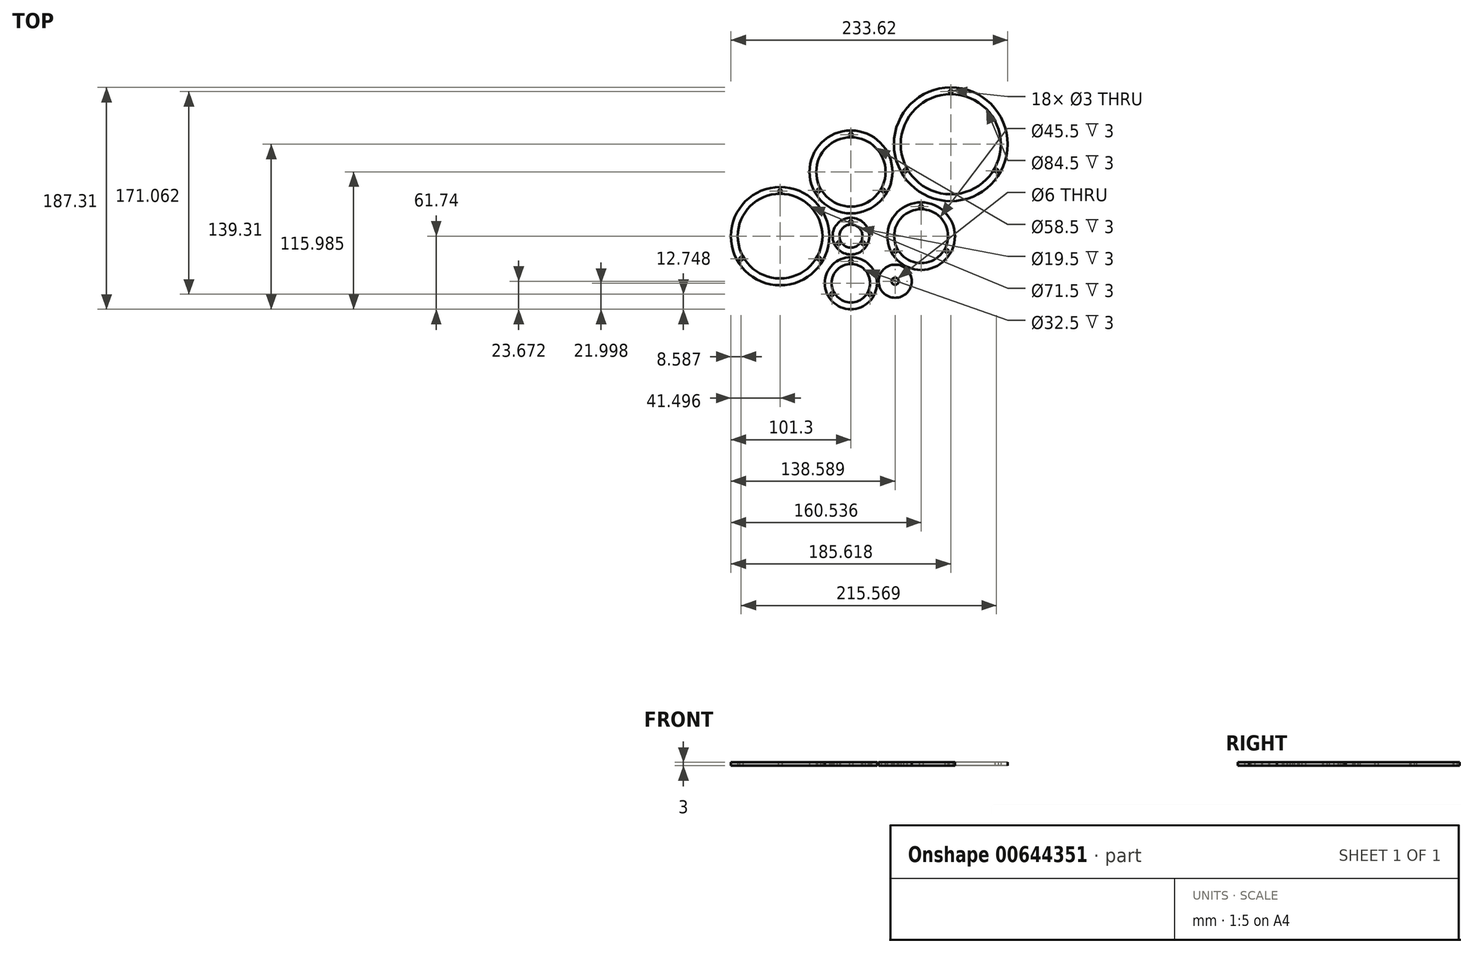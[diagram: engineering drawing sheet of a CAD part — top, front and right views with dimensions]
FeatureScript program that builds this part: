
annotation { "Feature Type Name" : "Feature", "Feature Type Description" : "" }
export const myFeature = defineFeature(function(context is Context, id is Id, definition is map)
    precondition{}
    {
        {
            var Q0;
            Q0=qCreatedBy(makeId("Top.planeOp"),FACE);
            var sketch = newSketch(context, id + "F0", { "sketchPlane" : qUnion([Q0])});
            skCircle(sketch, "E0", {"center": v(37.29, -38.07) * mm, "radius": 14 * mm});
            skCircle(sketch, "E1", {"center": v(37.29, -38.07) * mm, "radius": 3 * mm});
            skCircle(sketch, "E2", {"center": v(0, 0) * mm, "radius": 9.75 * mm});
            skCircle(sketch, "E3", {"center": v(0, 0) * mm, "radius": 15.5 * mm});
            skCircle(sketch, "E4", {"center": v(0, 12) * mm, "radius": 1.5 * mm});
            skCircle(sketch, "E5.1.0", {"center": v(-10.4, -6) * mm, "radius": 1.5 * mm});
            skCircle(sketch, "E5.2.0", {"center": v(10.4, -6) * mm, "radius": 1.5 * mm});
            skCircle(sketch, "E6", {"center": v(0, -39.74) * mm, "radius": 16.25 * mm});
            skCircle(sketch, "E7", {"center": v(0, -39.74) * mm, "radius": 22 * mm});
            skCircle(sketch, "E8", {"center": v(0, -21.24) * mm, "radius": 1.5 * mm});
            skCircle(sketch, "E9.1.0", {"center": v(-16.02, -49) * mm, "radius": 1.5 * mm});
            skCircle(sketch, "E9.2.0", {"center": v(16.02, -49) * mm, "radius": 1.5 * mm});
            skPoint(sketch, "E9.center", {"position": v(0, -42.38) * mm});
            skCircle(sketch, "E10", {"center": v(59.24, 0) * mm, "radius": 22.75 * mm});
            skCircle(sketch, "E11", {"center": v(59.24, 0) * mm, "radius": 28.5 * mm});
            skCircle(sketch, "E12", {"center": v(59.24, 25) * mm, "radius": 1.5 * mm});
            skCircle(sketch, "E13", {"center": v(0, 54.25) * mm, "radius": 29.25 * mm});
            skCircle(sketch, "E14", {"center": v(0, 54.25) * mm, "radius": 35 * mm});
            skCircle(sketch, "E15", {"center": v(0, 85.75) * mm, "radius": 1.5 * mm});
            skCircle(sketch, "E16", {"center": v(-59.8, 0) * mm, "radius": 35.75 * mm});
            skCircle(sketch, "E17", {"center": v(-59.8, 0) * mm, "radius": 41.5 * mm});
            skCircle(sketch, "E18", {"center": v(-59.8, 38) * mm, "radius": 1.5 * mm});
            skCircle(sketch, "E19", {"center": v(84.32, 77.57) * mm, "radius": 42.25 * mm});
            skCircle(sketch, "E20", {"center": v(84.32, 77.57) * mm, "radius": 48 * mm});
            skCircle(sketch, "E21", {"center": v(84.32, 122.07) * mm, "radius": 1.5 * mm});
            skCircle(sketch, "E22.1.0", {"center": v(37.59, -12.5) * mm, "radius": 1.5 * mm});
            skCircle(sketch, "E22.2.0", {"center": v(80.89, -12.5) * mm, "radius": 1.5 * mm});
            skCircle(sketch, "E23.1.0", {"center": v(45.78, 55.32) * mm, "radius": 1.5 * mm});
            skCircle(sketch, "E23.2.0", {"center": v(122.86, 55.32) * mm, "radius": 1.5 * mm});
            skCircle(sketch, "E24.1.0", {"center": v(-27.28, 38.5) * mm, "radius": 1.5 * mm});
            skCircle(sketch, "E24.2.0", {"center": v(27.28, 38.5) * mm, "radius": 1.5 * mm});
            skCircle(sketch, "E25.1.0", {"center": v(-92.71, -19) * mm, "radius": 1.5 * mm});
            skCircle(sketch, "E25.2.0", {"center": v(-26.9, -19) * mm, "radius": 1.5 * mm});
            skSolve(sketch);
        }
        {
            var Q0;
            Q0=makeQuery(id+"F0.imprint","IMPRINT",FACE,{"disambiguationData":[TD([[makeQuery(id+"F0.imprint","IMPRINT",EDGE,{"derivedFrom":sQuery(id+"F0.wireOp",EDGE,"E0")}),1.0]])]});
            var Q1;
            Q1=makeQuery(id+"F0.imprint","IMPRINT",FACE,{"disambiguationData":[TD([[makeQuery(id+"F0.imprint","IMPRINT",EDGE,{"derivedFrom":sQuery(id+"F0.wireOp",EDGE,"E6")}),-1.0]])]});
            var Q2;
            Q2=makeQuery(id+"F0.imprint","IMPRINT",FACE,{"disambiguationData":[TD([[makeQuery(id+"F0.imprint","IMPRINT",EDGE,{"derivedFrom":sQuery(id+"F0.wireOp",EDGE,"E16")}),-1.0]])]});
            var Q3;
            Q3=makeQuery(id+"F0.imprint","IMPRINT",FACE,{"disambiguationData":[TD([[makeQuery(id+"F0.imprint","IMPRINT",EDGE,{"derivedFrom":sQuery(id+"F0.wireOp",EDGE,"E2")}),-1.0]])]});
            var Q4;
            Q4=makeQuery(id+"F0.imprint","IMPRINT",FACE,{"disambiguationData":[TD([[makeQuery(id+"F0.imprint","IMPRINT",EDGE,{"derivedFrom":sQuery(id+"F0.wireOp",EDGE,"E10")}),-1.0]])]});
            var Q5;
            Q5=makeQuery(id+"F0.imprint","IMPRINT",FACE,{"disambiguationData":[TD([[makeQuery(id+"F0.imprint","IMPRINT",EDGE,{"derivedFrom":sQuery(id+"F0.wireOp",EDGE,"E13")}),-1.0]])]});
            var Q6;
            Q6=makeQuery(id+"F0.imprint","IMPRINT",FACE,{"disambiguationData":[TD([[makeQuery(id+"F0.imprint","IMPRINT",EDGE,{"derivedFrom":sQuery(id+"F0.wireOp",EDGE,"E19")}),-1.0]])]});
            extrude(context, id + "F1", {"entities" : qUnion([Q0, Q1, Q2, Q3, Q4, Q5, Q6]), "depth" : 3 * mm, "offsetDistance" : 25 * mm});
        }
    });
